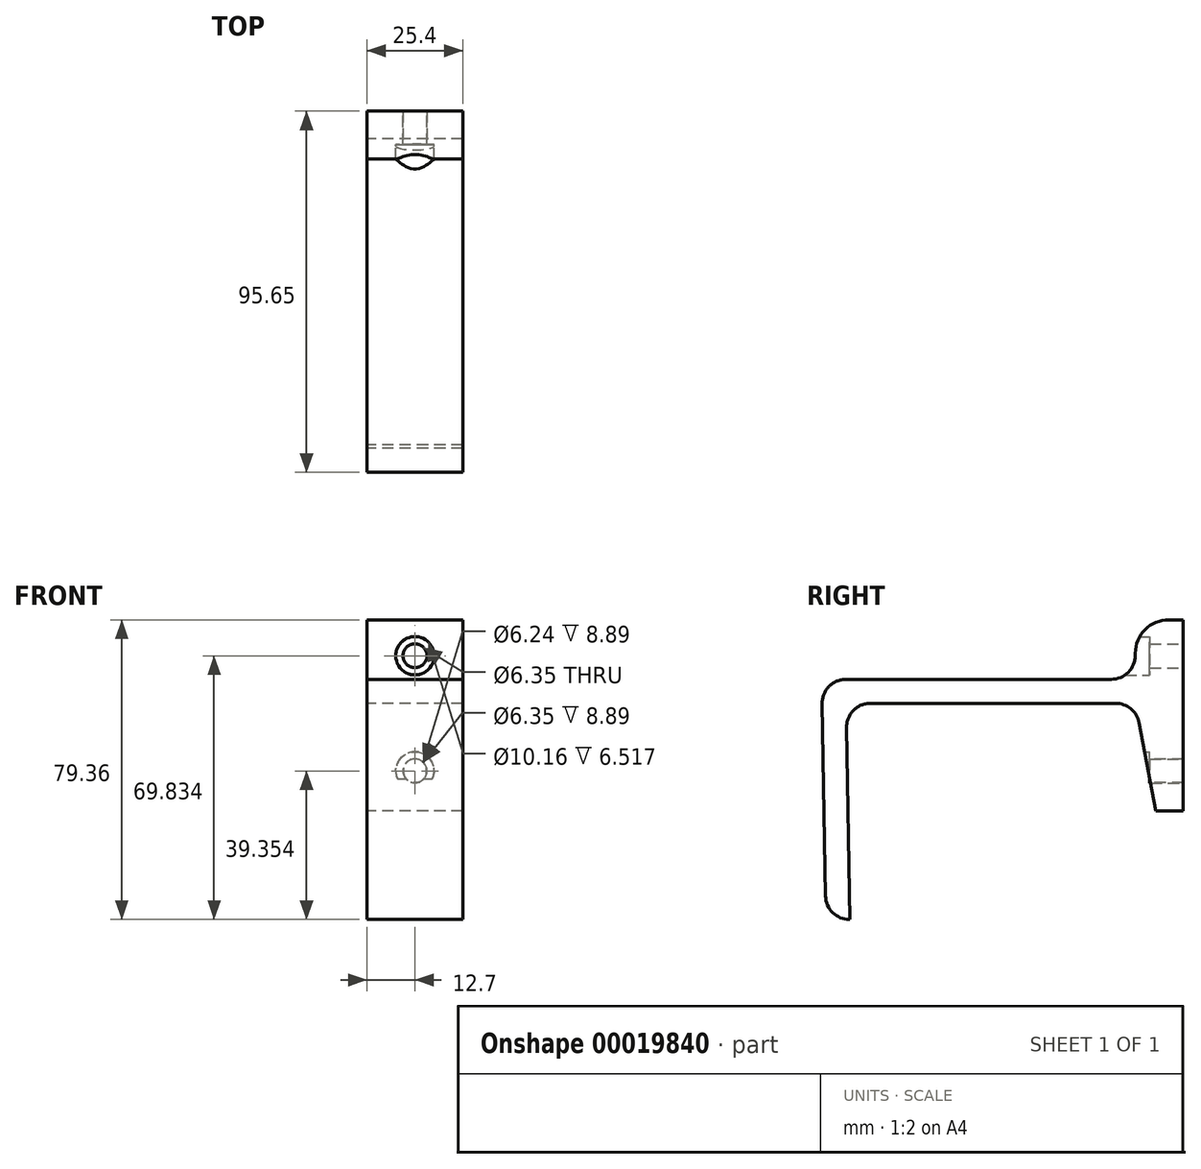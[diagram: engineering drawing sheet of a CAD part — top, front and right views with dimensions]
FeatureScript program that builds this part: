
annotation { "Feature Type Name" : "Feature", "Feature Type Description" : "" }
export const myFeature = defineFeature(function(context is Context, id is Id, definition is map)
    precondition{}
    {
        {
            var Q0;
            Q0=qCreatedBy(makeId("Right.planeOp"),FACE);
            var sketch = newSketch(context, id + "F0", { "sketchPlane" : qUnion([Q0])});
            skLineSegment(sketch, "E0", {"start": v(-37.37, -57.25) * mm, "end": v(-37.26, -57.25) * mm});
            skLineSegment(sketch, "E1", {"start": v(-37.26, -57.25) * mm, "end": v(-38.15, -6.46) * mm});
            skLineSegment(sketch, "E2", {"start": v(-31.8, 0) * mm, "end": v(33.09, 0) * mm});
            skLineSegment(sketch, "E3", {"start": v(39.32, -5.16) * mm, "end": v(43.77, -28.53) * mm});
            skLineSegment(sketch, "E4", {"start": v(43.77, -28.53) * mm, "end": v(51.04, -28.53) * mm});
            skLineSegment(sketch, "E5", {"start": v(51.04, -28.53) * mm, "end": v(51.04, 22.1) * mm});
            skLineSegment(sketch, "E6", {"start": v(51.04, 22.1) * mm, "end": v(38.34, 22.1) * mm});
            skLineSegment(sketch, "E7", {"start": v(38.34, 22.1) * mm, "end": v(38.34, 12.7) * mm});
            skLineSegment(sketch, "E8", {"start": v(32, 6.35) * mm, "end": v(-38.26, 6.35) * mm});
            skLineSegment(sketch, "E9", {"start": v(-44.6, -0.11) * mm, "end": v(-43.72, -51.01) * mm});
            skPoint(sketch, "E10.visualSharp", {"position": v(-38.26, 0) * mm});
            skArc(sketch, "E10.filletArc", {"start": v(-31.8, 0) * mm, "mid": v(-36.33, -1.9) * mm, "end": v(-38.15, -6.46) * mm});
            skPoint(sketch, "E11.visualSharp", {"position": v(38.34, 0) * mm});
            skArc(sketch, "E11.filletArc", {"start": v(39.32, -5.16) * mm, "mid": v(37.13, -1.46) * mm, "end": v(33.09, 0) * mm});
            skPoint(sketch, "E12.visualSharp", {"position": v(-44.72, 6.35) * mm});
            skArc(sketch, "E12.filletArc", {"start": v(-38.26, 6.35) * mm, "mid": v(-42.79, 4.45) * mm, "end": v(-44.6, -0.11) * mm});
            skPoint(sketch, "E13.visualSharp", {"position": v(-43.61, -57.25) * mm});
            skArc(sketch, "E13.filletArc", {"start": v(-43.72, -51.01) * mm, "mid": v(-41.82, -55.43) * mm, "end": v(-37.37, -57.25) * mm});
            skPoint(sketch, "E14.visualSharp", {"position": v(38.34, 6.35) * mm});
            skArc(sketch, "E14.filletArc", {"start": v(32, 6.35) * mm, "mid": v(36.48, 8.2) * mm, "end": v(38.34, 12.7) * mm});
            skLineSegment(sketch, "E15", {"start": v(-75.55, 0) * mm, "end": v(-57.62, 0) * mm, "construction": true});
            skSolve(sketch);
        }
        {
            var Q0;
            Q0=makeQuery(id+"F0.imprint","IMPRINT",FACE,{"disambiguationData":[TD([[makeQuery(id+"F0.imprint","IMPRINT",EDGE,{"derivedFrom":sQuery(id+"F0.wireOp",EDGE,"E1")}),1.0]])]});
            extrude(context, id + "F1", {"entities" : qUnion([Q0]), "depth" : 25.4 * mm});
        }
        {
            var Q0;
            Q0=makeQuery(id+"F1.opExtrude","SWEPT_EDGE",EDGE,{"disambiguationData":[OSD([sQuery(id+"F0.wireOp",EDGE,"E6"),sQuery(id+"F0.wireOp",EDGE,"E7")])]});
            fillet(context, id + "F2", {"entities" : qUnion([Q0]), "radius" : 8.9 * mm, "tangentPropagation" : true, "allowEdgeOverflow" : false});
        }
        {
            var Q0;
            Q0=makeQuery(id+"F1.opExtrude","SWEPT_FACE",FACE,{"disambiguationData":[OSD([sQuery(id+"F0.wireOp",EDGE,"E5")])]});
            var sketch = newSketch(context, id + "F3", { "sketchPlane" : qUnion([Q0])});
            skCircle(sketch, "E16", {"center": v(-12.7, -17.9) * mm, "radius": 3.18 * mm});
            skCircle(sketch, "E17", {"center": v(-12.7, 12.58) * mm, "radius": 3.18 * mm});
            skLineSegment(sketch, "E18", {"start": v(-12.7, 22.1) * mm, "end": v(-12.7, -28.53) * mm, "construction": true});
            skSolve(sketch);
        }
        {
            var Q0;
            Q0=makeQuery(id+"F3.imprint","IMPRINT",FACE,{"disambiguationData":[TD([[makeQuery(id+"F3.imprint","IMPRINT",EDGE,{"derivedFrom":sQuery(id+"F3.wireOp",EDGE,"E17")}),1.0]])]});
            var Q1;
            Q1=makeQuery(id+"F3.imprint","IMPRINT",FACE,{"disambiguationData":[TD([[makeQuery(id+"F3.imprint","IMPRINT",EDGE,{"derivedFrom":sQuery(id+"F3.wireOp",EDGE,"E16")}),1.0]])]});
            extrude(context, id + "F4", {"entities" : qUnion([Q0, Q1]), "operationType" : NewBodyOperationType.REMOVE, "oppositeDirection" : true, "depth" : 25.4 * mm});
        }
        {
            var Q0;
            Q0=makeQuery(id+"F1.opExtrude","SWEPT_FACE",FACE,{"disambiguationData":[OSD([sQuery(id+"F0.wireOp",EDGE,"E5")])]});
            var sketch = newSketch(context, id + "F5", { "sketchPlane" : qUnion([Q0])});
            skCircle(sketch, "E19", {"center": v(-12.7, 12.58) * mm, "radius": 3.18 * mm});
            skPoint(sketch, "E19.first.point", {"position": v(-14.2, 15.38) * mm});
            skPoint(sketch, "E19.second.point", {"position": v(-9.56, 13.08) * mm});
            skPoint(sketch, "E19.third.point", {"position": v(-12.34, 9.43) * mm});
            skCircle(sketch, "E20", {"center": v(-12.7, -17.9) * mm, "radius": 3.17 * mm});
            skPoint(sketch, "E20.first.point", {"position": v(-13.34, -14.79) * mm});
            skPoint(sketch, "E20.second.point", {"position": v(-9.97, -16.27) * mm});
            skPoint(sketch, "E20.third.point", {"position": v(-13.7, -20.91) * mm});
            skSolve(sketch);
        }
        {
            var Q0;
            Q0=makeQuery(id+"F5.imprint","IMPRINT",FACE,{"disambiguationData":[TD([[makeQuery(id+"F5.imprint","IMPRINT",EDGE,{"derivedFrom":sQuery(id+"F5.wireOp",EDGE,"E19")}),1.0]])]});
            var Q1;
            Q1=makeQuery(id+"F5.imprint","IMPRINT",FACE,{"disambiguationData":[TD([[makeQuery(id+"F5.imprint","IMPRINT",EDGE,{"derivedFrom":sQuery(id+"F5.wireOp",EDGE,"E20")}),1.0]])]});
            extrude(context, id + "F6", {"entities" : qUnion([Q0, Q1]), "oppositeDirection" : true, "depth" : 8.9 * mm});
        }
        {
            var Q0;
            Q0=makeQuery(id+"F6.opExtrude","CAP_FACE",FACE,{"disambiguationData":[OSD([sQuery(id+"F5.wireOp",EDGE,"E20")])],"isStart":false});
            var sketch = newSketch(context, id + "F7", { "sketchPlane" : qUnion([Q0])});
            skCircle(sketch, "E21", {"center": v(12.7, 12.58) * mm, "radius": 5.08 * mm});
            skCircle(sketch, "E22", {"center": v(12.7, -17.9) * mm, "radius": 5.08 * mm});
            skSolve(sketch);
        }
        {
            var Q0;
            Q0 = qSketchRegion(id + "F7", true);
            extrude(context, id + "F8", {"entities" : qUnion([Q0]), "operationType" : NewBodyOperationType.REMOVE, "depth" : 25.4 * mm});
        }
        {
            var Q0;
            Q0=makeQuery(id+"F6.opExtrude","CAP_FACE",FACE,{"disambiguationData":[OSD([sQuery(id+"F5.wireOp",EDGE,"E19")])],"isStart":false});
            var sketch = newSketch(context, id + "F9", { "sketchPlane" : qUnion([Q0])});
            skCircle(sketch, "E23", {"center": v(12.7, 12.58) * mm, "radius": 3.17 * mm});
            skPoint(sketch, "E23.first.point", {"position": v(9.54, 12.9) * mm});
            skPoint(sketch, "E23.second.point", {"position": v(10.54, 10.26) * mm});
            skPoint(sketch, "E23.third.point", {"position": v(11.75, 15.61) * mm});
            skCircle(sketch, "E24", {"center": v(12.7, -17.9) * mm, "radius": 3.12 * mm});
            skPoint(sketch, "E24.first.point", {"position": v(12, -14.85) * mm});
            skPoint(sketch, "E24.second.point", {"position": v(9.7, -18.78) * mm});
            skPoint(sketch, "E24.third.point", {"position": v(15.18, -19.8) * mm});
            skSolve(sketch);
        }
        {
            var Q0;
            Q0=makeQuery(id+"F9.imprint","IMPRINT",FACE,{"disambiguationData":[TD([[makeQuery(id+"F9.imprint","IMPRINT",EDGE,{"derivedFrom":sQuery(id+"F9.wireOp",EDGE,"E23")}),-1.0]])]});
            var Q1;
            Q1=makeQuery(id+"F9.imprint","IMPRINT",FACE,{"disambiguationData":[TD([[makeQuery(id+"F9.imprint","IMPRINT",EDGE,{"derivedFrom":sQuery(id+"F9.wireOp",EDGE,"E24")}),1.0]])]});
            extrude(context, id + "F10", {"entities" : qUnion([Q0, Q1]), "operationType" : NewBodyOperationType.REMOVE, "oppositeDirection" : true, "depth" : 25.4 * mm});
        }
    });
